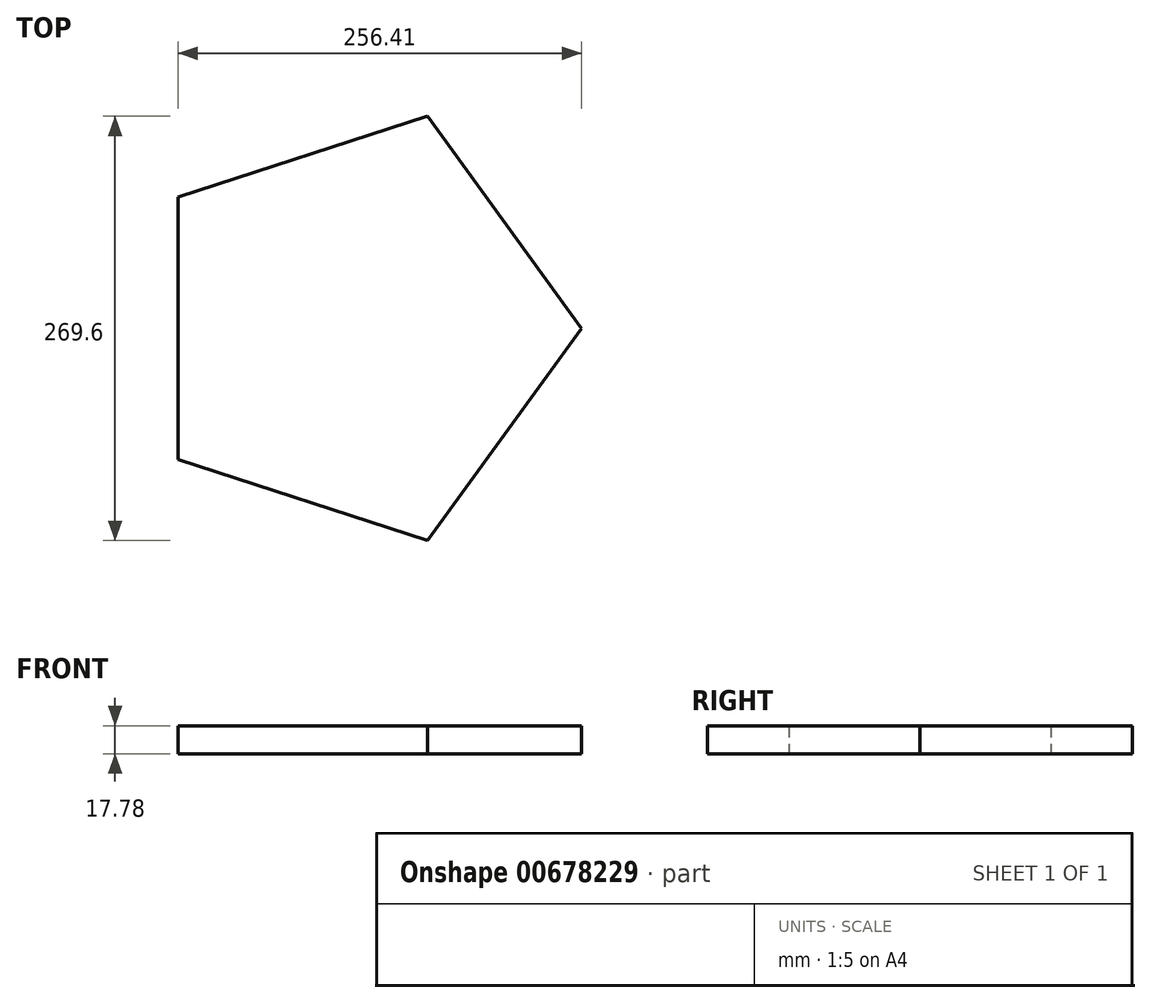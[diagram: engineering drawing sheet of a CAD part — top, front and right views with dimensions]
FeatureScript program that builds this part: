
annotation { "Feature Type Name" : "Feature", "Feature Type Description" : "" }
export const myFeature = defineFeature(function(context is Context, id is Id, definition is map)
    precondition{}
    {
        {
            var Q0;
            Q0=qCreatedBy(makeId("Top.planeOp"),FACE);
            var sketch = newSketch(context, id + "F0", { "sketchPlane" : qUnion([Q0])});
            skCircle(sketch, "E0.cCircle", {"center": v(0, 0) * mm, "radius": 114.67 * mm, "construction": true});
            skLineSegment(sketch, "E0.0", {"start": v(-114.67, -83.31) * mm, "end": v(-114.67, 83.31) * mm});
            skLineSegment(sketch, "E0.1", {"start": v(-114.67, 83.31) * mm, "end": v(43.8, 134.8) * mm});
            skLineSegment(sketch, "E0.2", {"start": v(43.8, 134.8) * mm, "end": v(141.74, 0) * mm});
            skLineSegment(sketch, "E0.3", {"start": v(141.74, 0) * mm, "end": v(43.8, -134.8) * mm});
            skLineSegment(sketch, "E0.4", {"start": v(43.8, -134.8) * mm, "end": v(-114.67, -83.31) * mm});
            skPoint(sketch, "E0.0.midPoint", {"position": v(-114.67, 0) * mm});
            skSolve(sketch);
        }
        {
            var Q0;
            Q0=makeQuery(id+"F0.imprint","IMPRINT",FACE,{"disambiguationData":[TD([[makeQuery(id+"F0.imprint","IMPRINT",EDGE,{"derivedFrom":sQuery(id+"F0.wireOp",EDGE,"E0.0")}),-1.0]])]});
            extrude(context, id + "F1", {"entities" : qUnion([Q0]), "depth" : 17.78 * mm, "offsetDistance" : 25.4 * mm});
        }
    });
